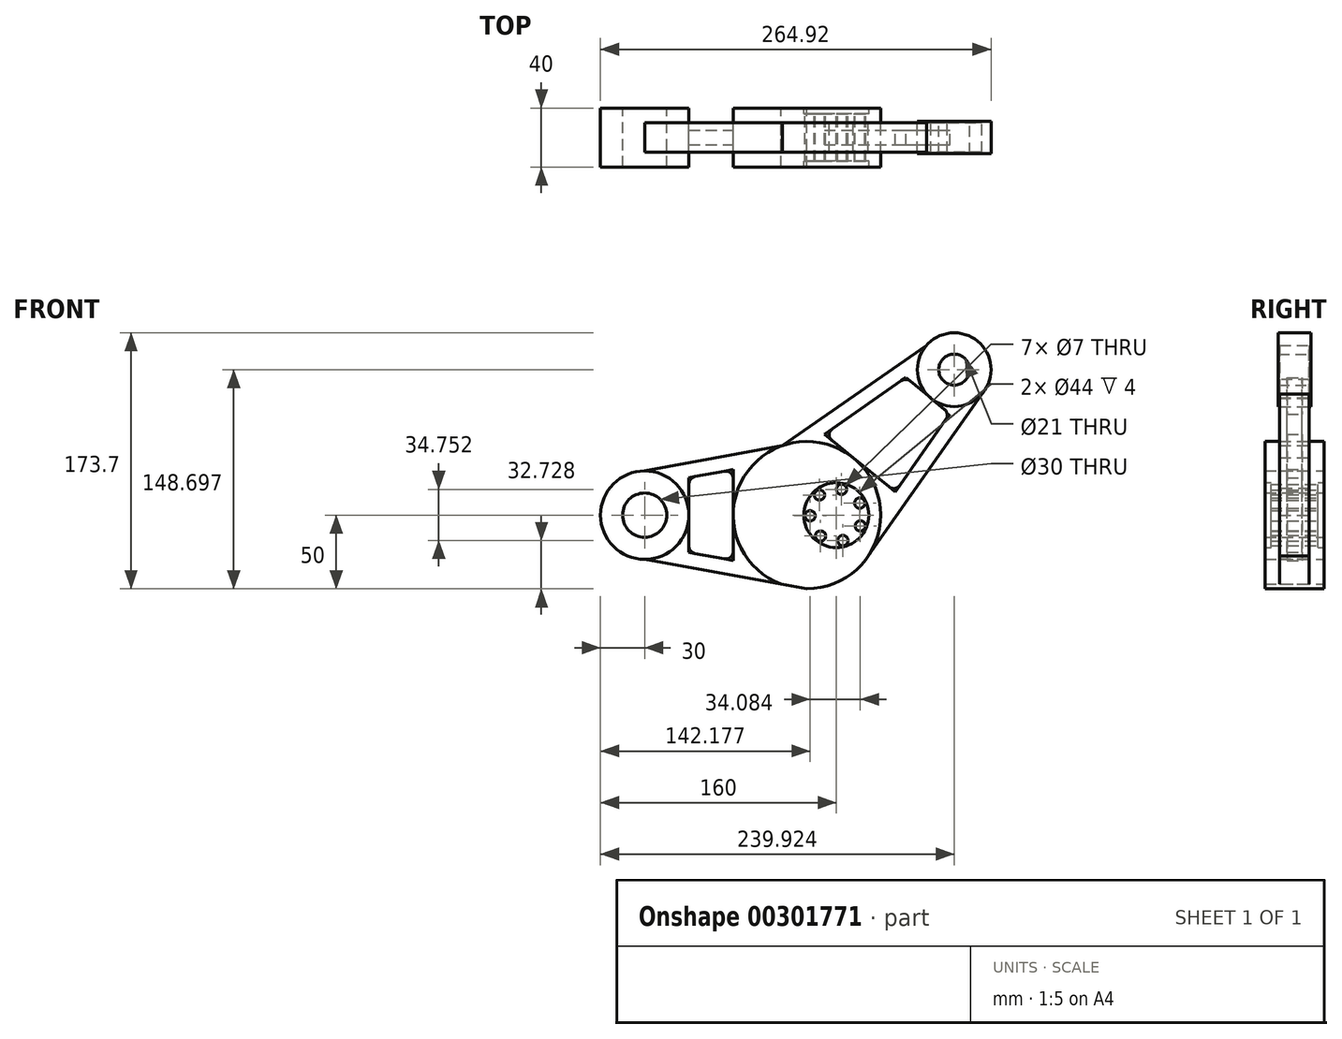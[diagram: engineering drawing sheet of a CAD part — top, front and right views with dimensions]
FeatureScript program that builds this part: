
annotation { "Feature Type Name" : "Feature", "Feature Type Description" : "" }
export const myFeature = defineFeature(function(context is Context, id is Id, definition is map)
    precondition{}
    {
        {
            var Q0;
            Q0=qCreatedBy(makeId("Front.planeOp"),FACE);
            var sketch = newSketch(context, id + "F0", { "sketchPlane" : qUnion([Q0])});
            skLineSegment(sketch, "E0", {"start": v(-130, 0) * mm, "end": v(0, 0) * mm});
            skLineSegment(sketch, "E1", {"start": v(0, 0) * mm, "end": v(79.92, 98.7) * mm});
            skCircle(sketch, "E2", {"center": v(79.92, 98.7) * mm, "radius": 10.5 * mm});
            skCircle(sketch, "E3", {"center": v(79.92, 98.7) * mm, "radius": 25 * mm});
            skCircle(sketch, "E4", {"center": v(-130, 0) * mm, "radius": 15 * mm});
            skCircle(sketch, "E5", {"center": v(-130, 0) * mm, "radius": 30 * mm});
            skPoint(sketch, "E6", {"position": v(-130, 30) * mm});
            skPoint(sketch, "E7", {"position": v(-20, 0) * mm});
            skCircle(sketch, "E8", {"center": v(-20, 0) * mm, "radius": 50 * mm});
            skPoint(sketch, "E9", {"position": v(61.2, 115.27) * mm});
            skPoint(sketch, "E10", {"position": v(-36.62, 47.16) * mm});
            skLineSegment(sketch, "E11", {"start": v(-130, 30) * mm, "end": v(-36.62, 47.16) * mm});
            skLineSegment(sketch, "E12", {"start": v(-36.62, 47.16) * mm, "end": v(61.2, 115.27) * mm});
            skLineSegment(sketch, "E13", {"start": v(-111.07, 23.3) * mm, "end": v(-57.41, 33.17) * mm});
            skLineSegment(sketch, "E14", {"start": v(-15.35, 49.78) * mm, "end": v(54.92, 98.71) * mm});
            skLineSegment(sketch, "E15", {"start": v(-130, -30) * mm, "end": v(-20, -50) * mm});
            skPoint(sketch, "E16", {"position": v(98.64, 82.12) * mm});
            skLineSegment(sketch, "E17", {"start": v(98.64, 82.12) * mm, "end": v(21.57, -27.78) * mm});
            skLineSegment(sketch, "E18", {"start": v(-111.07, -23.28) * mm, "end": v(-57.56, -33) * mm});
            skPoint(sketch, "E19.newPointA", {"position": v(-111.1, 23.3) * mm});
            skLineSegment(sketch, "E20", {"start": v(-111.1, 23.3) * mm, "end": v(-111.07, 23.3) * mm});
            skLineSegment(sketch, "E21", {"start": v(29.97, 1.62) * mm, "end": v(80.52, 73.7) * mm});
            skCircle(sketch, "E22", {"center": v(0, 0) * mm, "radius": 22 * mm});
            skPoint(sketch, "E23", {"position": v(-100, 0) * mm});
            skLineSegment(sketch, "E24", {"start": v(-100, -25.3) * mm, "end": v(-100, 25.34) * mm});
            skLineSegment(sketch, "E25", {"start": v(47.25, 93.37) * mm, "end": v(84.68, 62.21) * mm});
            skLineSegment(sketch, "E26", {"start": v(-70, 30.86) * mm, "end": v(-70, -30.75) * mm});
            skLineSegment(sketch, "E27", {"start": v(-8.18, 54.77) * mm, "end": v(39.93, 15.81) * mm});
            skLineSegment(sketch, "E28", {"start": v(0, 22) * mm, "end": v(0, -22) * mm});
            skCircle(sketch, "E29", {"center": v(-11.48, 13.64) * mm, "radius": 3.5 * mm});
            skCircle(sketch, "E30.1.0", {"center": v(-17.82, -0.47) * mm, "radius": 3.5 * mm});
            skCircle(sketch, "E30.2.0", {"center": v(-10.75, -14.23) * mm, "radius": 3.5 * mm});
            skCircle(sketch, "E30.3.0", {"center": v(4.42, -17.27) * mm, "radius": 3.5 * mm});
            skCircle(sketch, "E30.4.0", {"center": v(16.26, -7.31) * mm, "radius": 3.5 * mm});
            skCircle(sketch, "E30.5.0", {"center": v(15.86, 8.15) * mm, "radius": 3.5 * mm});
            skCircle(sketch, "E30.6.0", {"center": v(3.51, 17.48) * mm, "radius": 3.5 * mm});
            skSolve(sketch);
        }
        {
            var Q0;
            Q0=makeQuery(id+"F0.imprint","IMPRINT",FACE,{"disambiguationData":[TD([[makeQuery(id+"F0.imprint","IMPRINT",EDGE,{"derivedFrom":sQuery(id+"F0.wireOp",EDGE,"E4")}),-1.0]])]});
            var Q1;
            {var subQ0=sQuery(id+"F0.wireOp",EDGE,"E8");var subQ7=sQuery(id+"F0.wireOp",EDGE,"E0");var subQ8=makeQuery(id+"F0.imprint","INTERSECT",VERTEX,{"derivedFrom":[subQ7,subQ0]});Q1=makeQuery(id+"F0.imprint","IMPRINT",FACE,{"disambiguationData":[TD([[makeQuery(id+"F0.imprint","IMPRINT",EDGE,{"disambiguationData":[TD([[subQ8,-1.0]])],"derivedFrom":subQ7}),1.0]])]});}
            var Q2;
            {var subQ0=sQuery(id+"F0.wireOp",EDGE,"E8");var subQ2=sQuery(id+"F0.wireOp",EDGE,"E0");var subQ3=makeQuery(id+"F0.imprint","INTERSECT",VERTEX,{"derivedFrom":[subQ2,subQ0]});Q2=makeQuery(id+"F0.imprint","IMPRINT",FACE,{"disambiguationData":[TD([[makeQuery(id+"F0.imprint","IMPRINT",EDGE,{"disambiguationData":[TD([[subQ3,-1.0]])],"derivedFrom":subQ2}),-1.0]])]});}
            extrude(context, id + "F1", {"entities" : qUnion([Q0, Q1, Q2]), "endBound" : BoundingType.SYMMETRIC, "depth" : 40 * mm});
        }
        {
            var Q0;
            {var subQ1=sQuery(id+"F0.wireOp",EDGE,"E11");Q0=makeQuery(id+"F0.imprint","IMPRINT",FACE,{"disambiguationData":[TD([[makeQuery(id+"F0.imprint","IMPRINT",EDGE,{"derivedFrom":subQ1}),-1.0]])]});}
            var Q1;
            {var subQ3=sQuery(id+"F0.wireOp",EDGE,"E18");Q1=makeQuery(id+"F0.imprint","IMPRINT",FACE,{"disambiguationData":[TD([[makeQuery(id+"F0.imprint","IMPRINT",EDGE,{"derivedFrom":subQ3}),-1.0]])]});}
            var Q2;
            {var subQ0=sQuery(id+"F0.wireOp",EDGE,"E17");Q2=makeQuery(id+"F0.imprint","IMPRINT",FACE,{"disambiguationData":[TD([[makeQuery(id+"F0.imprint","IMPRINT",EDGE,{"derivedFrom":subQ0}),-1.0]])]});}
            var Q3;
            {var subQ0=sQuery(id+"F0.wireOp",EDGE,"E12");Q3=makeQuery(id+"F0.imprint","IMPRINT",FACE,{"disambiguationData":[TD([[makeQuery(id+"F0.imprint","IMPRINT",EDGE,{"derivedFrom":subQ0}),-1.0]])]});}
            var Q4;
            {var subQ0=sQuery(id+"F0.wireOp",EDGE,"E20");Q4=makeQuery(id+"F0.imprint","IMPRINT",FACE,{"disambiguationData":[TD([[makeQuery(id+"F0.imprint","IMPRINT",EDGE,{"derivedFrom":subQ0}),-1.0]])]});}
            var Q5;
            {var subQ0=sQuery(id+"F0.wireOp",EDGE,"E18");var subQ1=sQuery(id+"F0.wireOp",EDGE,"E5");var subQ2=makeQuery(id+"F0.imprint","INTERSECT",VERTEX,{"derivedFrom":[subQ1,subQ0]});Q5=makeQuery(id+"F0.imprint","IMPRINT",FACE,{"disambiguationData":[TD([[makeQuery(id+"F0.imprint","IMPRINT",EDGE,{"disambiguationData":[TD([[subQ2,-1.0]])],"derivedFrom":subQ0}),1.0]])]});}
            var Q6;
            {var subQ0=sQuery(id+"F0.wireOp",EDGE,"E14");var subQ1=sQuery(id+"F0.wireOp",EDGE,"E3");var subQ2=makeQuery(id+"F0.imprint","INTERSECT",VERTEX,{"derivedFrom":[subQ1,subQ0]});Q6=makeQuery(id+"F0.imprint","IMPRINT",FACE,{"disambiguationData":[TD([[makeQuery(id+"F0.imprint","IMPRINT",EDGE,{"disambiguationData":[TD([[subQ2,-1.0]])],"derivedFrom":subQ1}),-1.0]])]});}
            var Q7;
            {var subQ0=sQuery(id+"F0.wireOp",EDGE,"E3");var subQ1=sQuery(id+"F0.wireOp",EDGE,"E1");var subQ2=makeQuery(id+"F0.imprint","INTERSECT",VERTEX,{"derivedFrom":[subQ1,subQ0]});Q7=makeQuery(id+"F0.imprint","IMPRINT",FACE,{"disambiguationData":[TD([[makeQuery(id+"F0.imprint","IMPRINT",EDGE,{"disambiguationData":[TD([[subQ2,1.0]])],"derivedFrom":subQ1}),-1.0]])]});}
            var Q8;
            {var subQ4=sQuery(id+"F0.wireOp",EDGE,"E8");var subQ6=sQuery(id+"F0.wireOp",EDGE,"E17");var subQ7=makeQuery(id+"F0.imprint","INTERSECT",VERTEX,{"derivedFrom":[subQ4,subQ6]});Q8=makeQuery(id+"F0.imprint","IMPRINT",FACE,{"disambiguationData":[TD([[makeQuery(id+"F0.imprint","IMPRINT",EDGE,{"disambiguationData":[TD([[subQ7,-1.0]])],"derivedFrom":subQ4}),-1.0]])]});}
            var Q9;
            {var subQ0=sQuery(id+"F0.wireOp",EDGE,"E13");var subQ1=sQuery(id+"F0.wireOp",EDGE,"E8");var subQ2=makeQuery(id+"F0.imprint","INTERSECT",VERTEX,{"derivedFrom":[subQ1,subQ0]});Q9=makeQuery(id+"F0.imprint","IMPRINT",FACE,{"disambiguationData":[TD([[makeQuery(id+"F0.imprint","IMPRINT",EDGE,{"disambiguationData":[TD([[subQ2,1.0]])],"derivedFrom":subQ0}),-1.0]])]});}
            var Q10;
            {var subQ0=sQuery(id+"F0.wireOp",EDGE,"E18");var subQ1=sQuery(id+"F0.wireOp",EDGE,"E8");var subQ2=makeQuery(id+"F0.imprint","INTERSECT",VERTEX,{"derivedFrom":[subQ1,subQ0]});Q10=makeQuery(id+"F0.imprint","IMPRINT",FACE,{"disambiguationData":[TD([[makeQuery(id+"F0.imprint","IMPRINT",EDGE,{"disambiguationData":[TD([[subQ2,1.0]])],"derivedFrom":subQ0}),1.0]])]});}
            var Q11;
            {var subQ0=sQuery(id+"F0.wireOp",EDGE,"E8");var subQ1=sQuery(id+"F0.wireOp",EDGE,"E1");var subQ2=makeQuery(id+"F0.imprint","INTERSECT",VERTEX,{"derivedFrom":[subQ1,subQ0]});Q11=makeQuery(id+"F0.imprint","IMPRINT",FACE,{"disambiguationData":[TD([[makeQuery(id+"F0.imprint","IMPRINT",EDGE,{"disambiguationData":[TD([[subQ2,-1.0]])],"derivedFrom":subQ1}),-1.0]])]});}
            var Q12;
            {var subQ0=sQuery(id+"F0.wireOp",EDGE,"E14");var subQ1=sQuery(id+"F0.wireOp",EDGE,"E8");var subQ2=makeQuery(id+"F0.imprint","INTERSECT",VERTEX,{"derivedFrom":[subQ1,subQ0]});Q12=makeQuery(id+"F0.imprint","IMPRINT",FACE,{"disambiguationData":[TD([[makeQuery(id+"F0.imprint","IMPRINT",EDGE,{"disambiguationData":[TD([[subQ2,1.0]])],"derivedFrom":subQ1}),-1.0]])]});}
            var Q13;
            {var subQ0=sQuery(id+"F0.wireOp",EDGE,"E8");var subQ1=sQuery(id+"F0.wireOp",EDGE,"E1");var subQ2=makeQuery(id+"F0.imprint","INTERSECT",VERTEX,{"derivedFrom":[subQ1,subQ0]});Q13=makeQuery(id+"F0.imprint","IMPRINT",FACE,{"disambiguationData":[TD([[makeQuery(id+"F0.imprint","IMPRINT",EDGE,{"disambiguationData":[TD([[subQ2,-1.0]])],"derivedFrom":subQ1}),1.0]])]});}
            extrude(context, id + "F2", {"entities" : qUnion([Q0, Q1, Q2, Q3, Q4, Q5, Q6, Q7, Q8, Q9, Q10, Q11, Q12, Q13]), "endBound" : BoundingType.SYMMETRIC, "depth" : 20 * mm});
        }
        {
            var Q0;
            Q0=makeQuery(id+"F0.imprint","IMPRINT",FACE,{"disambiguationData":[TD([[makeQuery(id+"F0.imprint","IMPRINT",EDGE,{"derivedFrom":sQuery(id+"F0.wireOp",EDGE,"E2")}),-1.0]])]});
            extrude(context, id + "F3", {"entities" : qUnion([Q0]), "endBound" : BoundingType.SYMMETRIC, "depth" : 22 * mm});
        }
        {
            var Q0;
            {var subQ0=sQuery(id+"F0.wireOp",EDGE,"E1");var subQ1=sQuery(id+"F0.wireOp",EDGE,"E0");var subQ2=makeQuery(id+"F0.imprint","INTERSECT",VERTEX,{"derivedFrom":[subQ1,subQ0]});Q0=makeQuery(id+"F0.imprint","IMPRINT",FACE,{"disambiguationData":[TD([[makeQuery(id+"F0.imprint","IMPRINT",EDGE,{"disambiguationData":[TD([[subQ2,1.0]])],"derivedFrom":subQ1}),-1.0]])]});}
            var Q1;
            {var subQ0=sQuery(id+"F0.wireOp",EDGE,"E1");var subQ1=sQuery(id+"F0.wireOp",EDGE,"E0");var subQ2=makeQuery(id+"F0.imprint","INTERSECT",VERTEX,{"derivedFrom":[subQ1,subQ0]});Q1=makeQuery(id+"F0.imprint","IMPRINT",FACE,{"disambiguationData":[TD([[makeQuery(id+"F0.imprint","IMPRINT",EDGE,{"disambiguationData":[TD([[subQ2,1.0]])],"derivedFrom":subQ1}),1.0]])]});}
            var Q2;
            {var subQ3=sQuery(id+"F0.wireOp",EDGE,"qnJONYtE-kARB-re2H-ICBy-ppyqnEnGbyeU");Q2=makeQuery(id+"F0.imprint","IMPRINT",FACE,{"disambiguationData":[TD([[makeQuery(id+"F0.imprint","IMPRINT",EDGE,{"derivedFrom":subQ3}),-1.0]])]});}
            var Q3;
            Q3=makeQuery(id+"F0.imprint","IMPRINT",FACE,{"disambiguationData":[TD([[makeQuery(id+"F0.imprint","IMPRINT",EDGE,{"derivedFrom":sQuery(id+"F0.wireOp",EDGE,"ucIOyzIV-9jeF-NNun-mkZD-NYEJTpAPcb5Y")}),-1.0]])]});
            var Q4;
            Q4=makeQuery(id+"F0.imprint","IMPRINT",FACE,{"disambiguationData":[TD([[makeQuery(id+"F0.imprint","IMPRINT",EDGE,{"derivedFrom":sQuery(id+"F0.wireOp",EDGE,"E30.6.0")}),-1.0]])]});
            var Q5;
            Q5=makeQuery(id+"F0.imprint","IMPRINT",FACE,{"disambiguationData":[TD([[makeQuery(id+"F0.imprint","IMPRINT",EDGE,{"derivedFrom":sQuery(id+"F0.wireOp",EDGE,"E30.3.0")}),-1.0]])]});
            extrude(context, id + "F4", {"entities" : qUnion([Q0, Q1, Q2, Q3, Q4, Q5]), "operationType" : NewBodyOperationType.ADD, "endBound" : BoundingType.SYMMETRIC, "depth" : 32 * mm});
        }
        {
            var Q0;
            Q0=makeQuery(id+"F2.opExtrude","SWEPT_EDGE",EDGE,{"disambiguationData":[OSD([sQuery(id+"F0.wireOp",EDGE,"E18"),sQuery(id+"F0.wireOp",EDGE,"E24")])]});
            var Q1;
            Q1=makeQuery(id+"F2.opExtrude","SWEPT_EDGE",EDGE,{"disambiguationData":[OSD([sQuery(id+"F0.wireOp",EDGE,"E13"),sQuery(id+"F0.wireOp",EDGE,"E24")])]});
            var Q2;
            Q2=makeQuery(id+"F2.opExtrude","SWEPT_EDGE",EDGE,{"disambiguationData":[OSD([sQuery(id+"F0.wireOp",EDGE,"E21"),sQuery(id+"F0.wireOp",EDGE,"E25")])]});
            var Q3;
            Q3=makeQuery(id+"F2.opExtrude","SWEPT_EDGE",EDGE,{"disambiguationData":[OSD([sQuery(id+"F0.wireOp",EDGE,"E14"),sQuery(id+"F0.wireOp",EDGE,"E25")])]});
            var Q4;
            Q4=makeQuery(id+"F2.opExtrude","SWEPT_EDGE",EDGE,{"disambiguationData":[OSD([sQuery(id+"F0.wireOp",EDGE,"E14"),sQuery(id+"F0.wireOp",EDGE,"E27")])]});
            var Q5;
            Q5=makeQuery(id+"F2.opExtrude","SWEPT_EDGE",EDGE,{"disambiguationData":[OSD([sQuery(id+"F0.wireOp",EDGE,"E18"),sQuery(id+"F0.wireOp",EDGE,"E26")])]});
            var Q6;
            Q6=makeQuery(id+"F2.opExtrude","SWEPT_EDGE",EDGE,{"disambiguationData":[OSD([sQuery(id+"F0.wireOp",EDGE,"E13"),sQuery(id+"F0.wireOp",EDGE,"E26")])]});
            var Q7;
            Q7=makeQuery(id+"F2.opExtrude","SWEPT_EDGE",EDGE,{"disambiguationData":[OSD([sQuery(id+"F0.wireOp",EDGE,"E21"),sQuery(id+"F0.wireOp",EDGE,"E27")])]});
            fillet(context, id + "F5", {"entities" : qUnion([Q0, Q1, Q2, Q3, Q4, Q5, Q6, Q7]), "radius" : 5 * mm, "tangentPropagation" : true, "allowEdgeOverflow" : false});
        }
        {
            var Q0;
            {var subQ0=sQuery(id+"F0.wireOp",EDGE,"E24");var subQ5=sQuery(id+"F0.wireOp",EDGE,"E13");var subQ6=makeQuery(id+"F0.imprint","INTERSECT",VERTEX,{"derivedFrom":[subQ5,subQ0]});Q0=makeQuery(id+"F0.imprint","IMPRINT",FACE,{"disambiguationData":[TD([[makeQuery(id+"F0.imprint","IMPRINT",EDGE,{"disambiguationData":[TD([[subQ6,-1.0]])],"derivedFrom":subQ5}),-1.0]])]});}
            var Q1;
            {var subQ0=sQuery(id+"F0.wireOp",EDGE,"E24");var subQ5=sQuery(id+"F0.wireOp",EDGE,"E18");var subQ6=makeQuery(id+"F0.imprint","INTERSECT",VERTEX,{"derivedFrom":[subQ5,subQ0]});Q1=makeQuery(id+"F0.imprint","IMPRINT",FACE,{"disambiguationData":[TD([[makeQuery(id+"F0.imprint","IMPRINT",EDGE,{"disambiguationData":[TD([[subQ6,-1.0]])],"derivedFrom":subQ5}),1.0]])]});}
            var Q2;
            {var subQ4=sQuery(id+"F0.wireOp",EDGE,"E1");var subQ6=sQuery(id+"F0.wireOp",EDGE,"E27");var subQ8=makeQuery(id+"F0.imprint","INTERSECT",VERTEX,{"derivedFrom":[subQ4,subQ6]});Q2=makeQuery(id+"F0.imprint","IMPRINT",FACE,{"disambiguationData":[TD([[makeQuery(id+"F0.imprint","IMPRINT",EDGE,{"disambiguationData":[TD([[subQ8,-1.0]])],"derivedFrom":subQ4}),1.0]])]});}
            var Q3;
            {var subQ0=sQuery(id+"F0.wireOp",EDGE,"E27");var subQ1=sQuery(id+"F0.wireOp",EDGE,"E1");var subQ2=makeQuery(id+"F0.imprint","INTERSECT",VERTEX,{"derivedFrom":[subQ1,subQ0]});Q3=makeQuery(id+"F0.imprint","IMPRINT",FACE,{"disambiguationData":[TD([[makeQuery(id+"F0.imprint","IMPRINT",EDGE,{"disambiguationData":[TD([[subQ2,-1.0]])],"derivedFrom":subQ1}),-1.0]])]});}
            extrude(context, id + "F6", {"entities" : qUnion([Q0, Q1, Q2, Q3]), "endBound" : BoundingType.SYMMETRIC, "depth" : 10 * mm});
        }
    });
